# Revit family: KDW010034
name_source: partatom
category: Plumbing Fixtures
revit_build: Autodesk Revit 2015 (Build: 20140606_1530(x64)
units: mm (PartAtom-declared; Revit-internal decimal feet)

## types (1)
- KDW010034
    Accessory = Yes
    BIMobject category = Bath & Spas
    Brand url = http://www.kaldewei.com
    Chrome = Chrome
    Color = https://www.kaldewei.co.uk
    ColourOptions = https://www.kaldewei.co.uk
    ConnectingDimensions = EN 232
    Design country = Germany
    DrainSize = 52 mm
    Durability = https://www.kaldewei.de
    Edition number = 1
    Features = https://www.kaldewei.co.uk
    Finish = https://www.kaldewei.co.uk
    Finition = Kaldewei
    HasGrabHandles = https://www.kaldewei.co.uk
    IFC Classification = Furnishing Element
    IfcExportAs = BATH
    IfcExportType = IfcSanitaryTerminalType
    IntegralAccessories = https://www.kaldewei.co.uk
    Manufacturer = Kaldewei
    Manufacturer country = Germany
    ManufacturerCountry = GERMANY
    ManufacturerName = KALDEWEI
    ManufacturerURL = https://www.kaldewei.com
    Material = steel enamel
    Material main = Steel
    Material secondary = Enamel
    Model = PURO MIT SEITLICHEM ÜBERLAUF
    NBS Reference Code = 35-06-08
    NBS Reference Description = Baths
    Name = PURO with side overflow
    Nominal height = 750 cm
    Nominal width = 1700 cm
    NominalDepth = 420
    NominalLength = 1700
    ObjectName = PURO with side overflow 750x1700x420
    ObjectNorm = EN 14516EU DECLARATION OF PERFORMANCE(https://www.kaldewei.de
    ObjectPicture = https://www.kaldewei.co.uk
    ObjectURL = https://www.kaldewei.co.uk
    Polantis code = KDW010034
    Product Guid = bbb6ff2f-9647-4d52-b169-1153387432ea
    Product SKU = 656
    Product certification = https://www.kaldewei.co.uk
    Product data url = https://bimobject.com
    Product family = PURO
    Product group = Bathtub
    Product url = https://www.kaldewei.co.uk
    ProductInformation = Model No.656: Reducing all elements to their basic essence is one of the guiding principles of modern architecture and interior design. The same principle applies to the clear, purist design of the PURO bath. The PURO has an especially generous interior length for the ultimate in bathing comfort.
    QR code = http://bimobject.com
    Revision = 1
    SerialNumber = 656
    Shape = Rectangular baths
    Size = 750x1700x420
    SupportFrame = https://www.kaldewei.co.uk
    Sustainability = https://kaldewei-fa.secure.footprint.net
    Technical description = https://www.kaldewei.co.uk
    TechnicalDataURL = https://kaldewei.typo-live.web-factory.de
    Type Comments = PURO MIT SEITLICHEM ÜBERLAUF 656 750x1700x420
    UNSPSC Code = 30181501
    UNSPSCCode = 30181500
    UNSPSCNames = Sanitary ware
    URL = https://www.kaldewei.co.uk
    Uniclass 1.4 Code = L7211
    Uniclass 1.4 Description = Baths
    Uniclass 2.0 Code = PR-35-06-08
    Uniclass 2.0 Description = Baths
    Uniclass 2015 = Pr_40_20_06_08
    Version = 5
    VolumeToOverflowMaximum = 137
    WarrantyDurationParts = 30
    WarrantyDurationUnit = Year
    WarrantyStartDate = https://www.kaldewei.co.uk
    WaterSupplyOverflowAndWasteHolesOverflow = 52 mm
    WaterSupplyOverflowAndWasteHolesWaste = 52 mm
    Weight = 51
    Weight Net (Kg) = 51

## geometry (parser evidence)
native form markers: Sweep x10
no freeform markers — native parametric forms only
